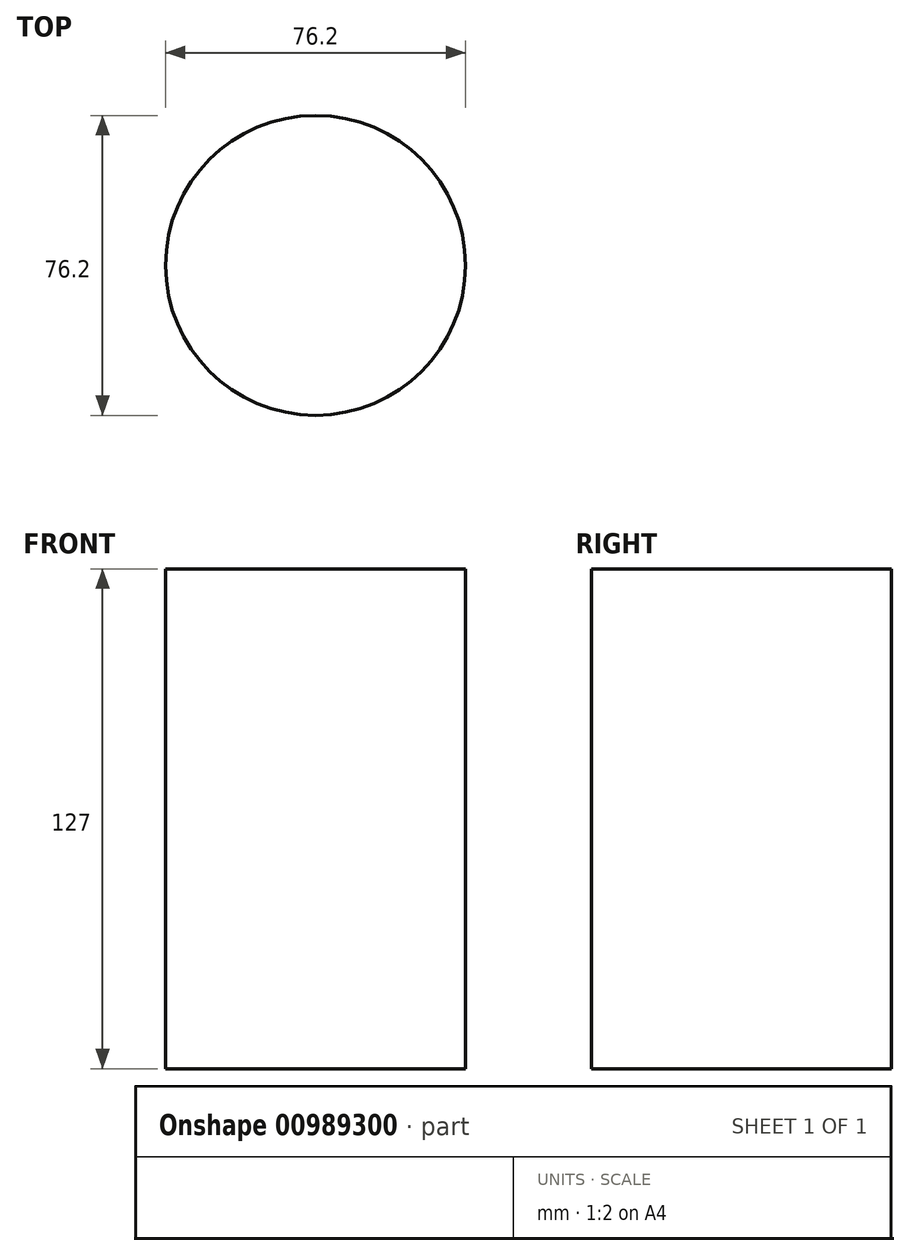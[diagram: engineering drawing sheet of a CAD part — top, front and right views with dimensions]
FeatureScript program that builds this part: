
annotation { "Feature Type Name" : "Feature", "Feature Type Description" : "" }
export const myFeature = defineFeature(function(context is Context, id is Id, definition is map)
    precondition{}
    {
        {
            var Q0;
            Q0=qCreatedBy(makeId("Top.planeOp"),FACE);
            var sketch = newSketch(context, id + "F0", { "sketchPlane" : qUnion([Q0])});
            skCircle(sketch, "E0", {"center": v(0, 0) * mm, "radius": 38.1 * mm});
            skSolve(sketch);
        }
        {
            var Q0;
            Q0 = qSketchRegion(id + "F0", true);
            extrude(context, id + "F1", {"entities" : qUnion([Q0]), "depth" : 127 * mm, "offsetDistance" : 25.4 * mm});
        }
    });
